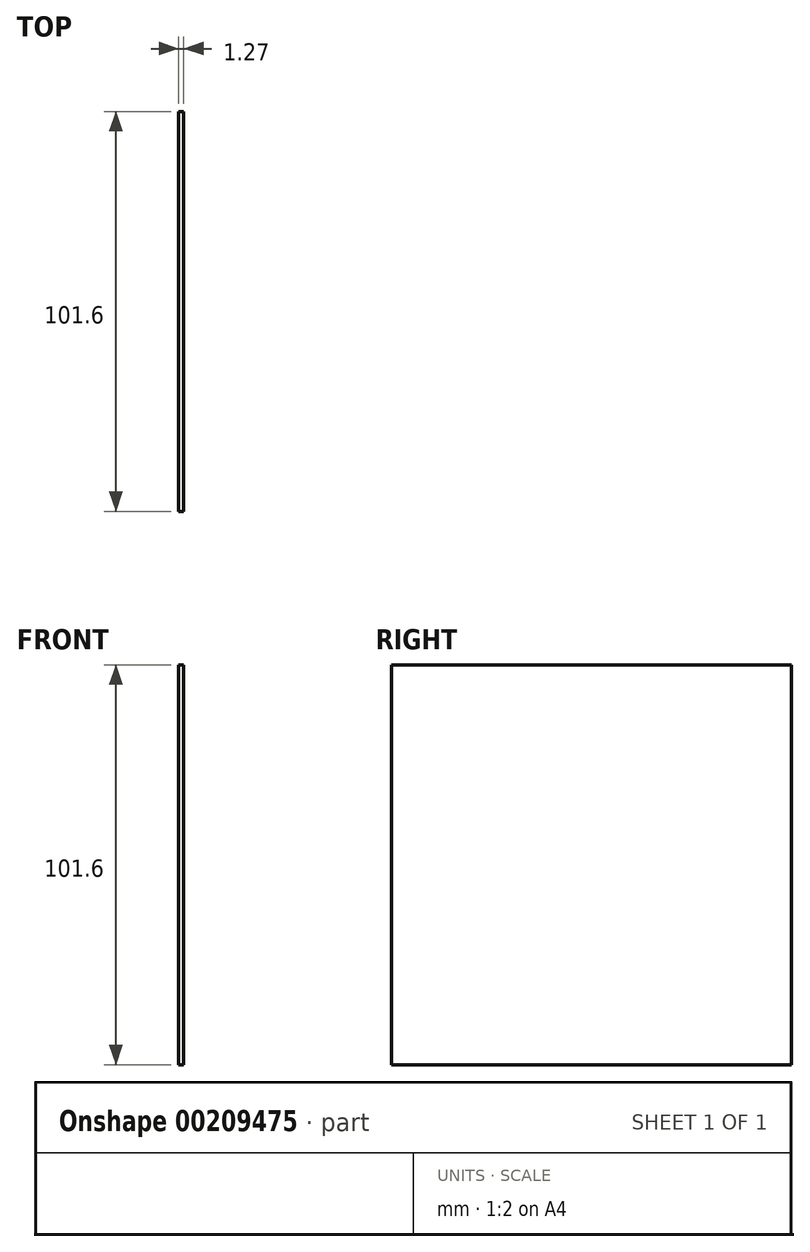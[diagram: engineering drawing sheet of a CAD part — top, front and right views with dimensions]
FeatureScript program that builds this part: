
annotation { "Feature Type Name" : "Feature", "Feature Type Description" : "" }
export const myFeature = defineFeature(function(context is Context, id is Id, definition is map)
    precondition{}
    {
        {
            var Q0;
            Q0=qCreatedBy(makeId("Right.planeOp"),FACE);
            var sketch = newSketch(context, id + "F0", { "sketchPlane" : qUnion([Q0])});
            skLineSegment(sketch, "E0.bottom", {"start": v(50.8, 50.8) * mm, "end": v(-50.8, 50.8) * mm});
            skLineSegment(sketch, "E0.top", {"start": v(50.8, -50.8) * mm, "end": v(-50.8, -50.8) * mm});
            skLineSegment(sketch, "E0.left", {"start": v(50.8, 50.8) * mm, "end": v(50.8, -50.8) * mm});
            skLineSegment(sketch, "E0.right", {"start": v(-50.8, 50.8) * mm, "end": v(-50.8, -50.8) * mm});
            skPoint(sketch, "E0.middle", {"position": v(0, 0) * mm});
            skSolve(sketch);
        }
        {
            var Q0;
            Q0 = qSketchRegion(id + "F0", true);
            extrude(context, id + "F1", {"entities" : qUnion([Q0]), "depth" : 1.27 * mm, "offsetDistance" : 25.4 * mm});
        }
    });
